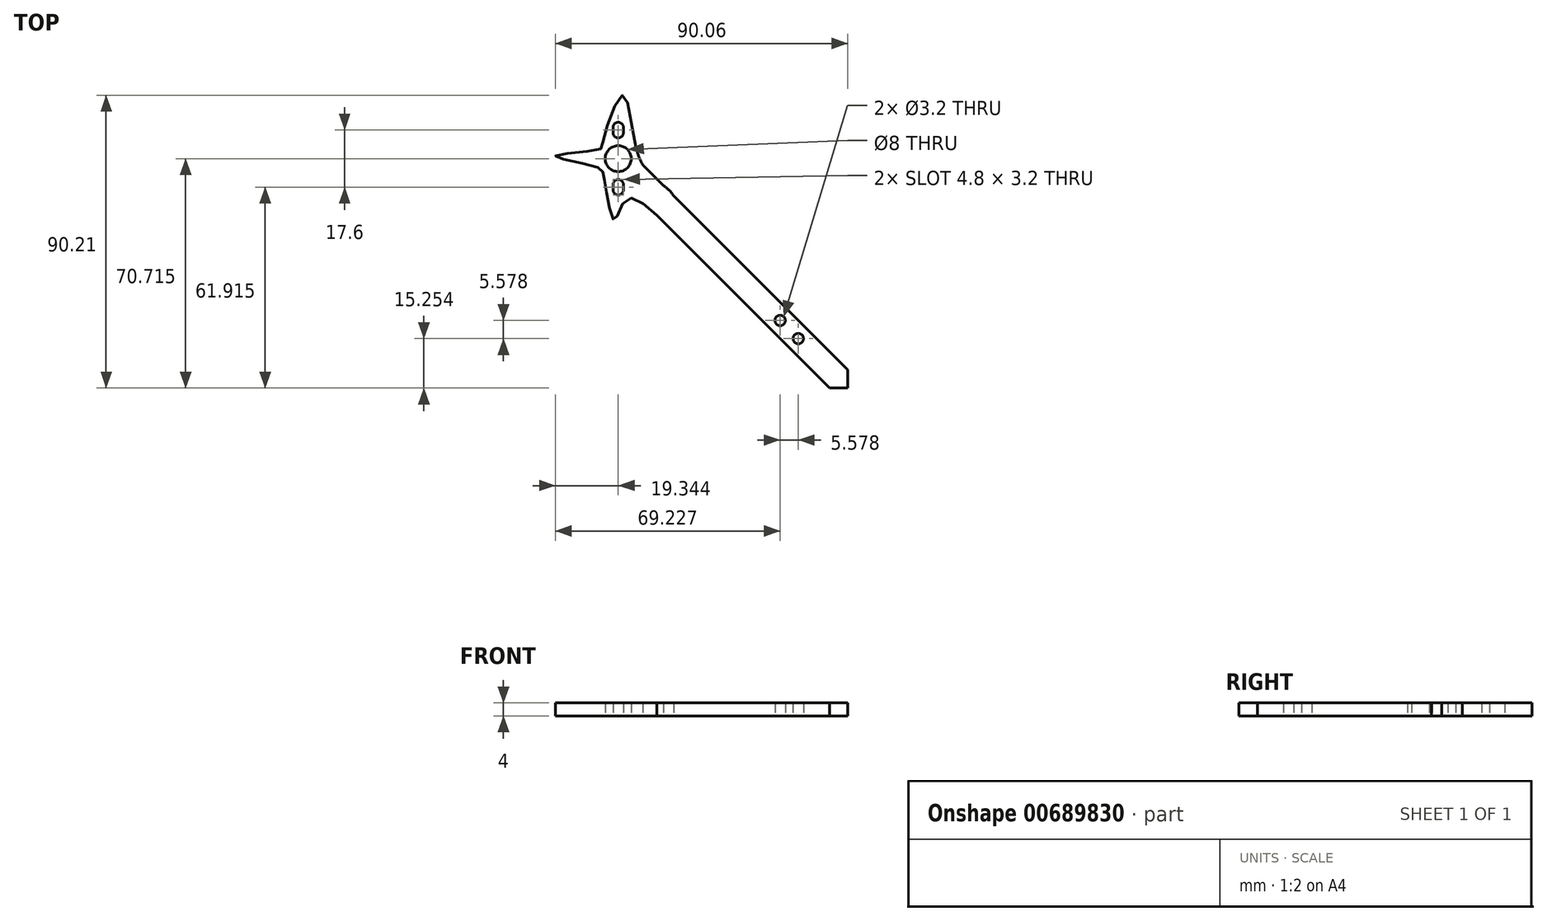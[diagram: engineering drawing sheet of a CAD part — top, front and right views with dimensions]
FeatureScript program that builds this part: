
annotation { "Feature Type Name" : "Feature", "Feature Type Description" : "" }
export const myFeature = defineFeature(function(context is Context, id is Id, definition is map)
    precondition{}
    {
        {
            var Q0;
            Q0=qCreatedBy(makeId("Top.planeOp"),FACE);
            var sketch = newSketch(context, id + "F0", { "sketchPlane" : qUnion([Q0])});
            skLineSegment(sketch, "E0.MirrorCS", {"start": v(4.18, -0.18) * mm, "end": v(-6.4, 10.4) * mm});
            skLineSegment(sketch, "E1.1", {"start": v(4.18, 5.48) * mm, "end": v(-45.9, 55.55) * mm});
            skLineSegment(sketch, "E2.0", {"start": v(-1.48, -0.18) * mm, "end": v(-51.15, 49.49) * mm});
            skCircle(sketch, "E3", {"center": v(-13.11, 17.11) * mm, "radius": 1.6 * mm});
            skCircle(sketch, "E4.MirrorC", {"center": v(-7.53, 11.53) * mm, "radius": 1.6 * mm});
            skLineSegment(sketch, "E5.trimOffspring", {"start": v(-8.67, 12.67) * mm, "end": v(-11.98, 15.98) * mm});
            skCircle(sketch, "E6", {"center": v(-63, 67) * mm, "radius": 4 * mm});
            skArc(sketch, "E7", {"start": v(-61.4, 76.6) * mm, "mid": v(-63, 78.2) * mm, "end": v(-64.6, 76.6) * mm});
            skArc(sketch, "E8", {"start": v(-64.6, 57.4) * mm, "mid": v(-63, 55.8) * mm, "end": v(-61.4, 57.4) * mm});
            skPoint(sketch, "E9", {"position": v(-64.6, 76.6) * mm});
            skPoint(sketch, "E10", {"position": v(-61.4, 76.6) * mm});
            skPoint(sketch, "E11", {"position": v(-61.4, 57.4) * mm});
            skPoint(sketch, "E12", {"position": v(-64.6, 57.4) * mm});
            skPoint(sketch, "E13", {"position": v(-63, 75) * mm});
            skPoint(sketch, "E14", {"position": v(-63, 59) * mm});
            skArc(sketch, "E15", {"start": v(-61.4, 59) * mm, "mid": v(-63, 60.6) * mm, "end": v(-64.6, 59) * mm});
            skArc(sketch, "E16", {"start": v(-64.6, 75) * mm, "mid": v(-63, 73.4) * mm, "end": v(-61.4, 75) * mm});
            skPoint(sketch, "E17", {"position": v(-64.6, 75) * mm});
            skPoint(sketch, "E18", {"position": v(-61.4, 75) * mm});
            skLineSegment(sketch, "E19", {"start": v(-64.6, 75) * mm, "end": v(-64.6, 76.6) * mm});
            skLineSegment(sketch, "E20", {"start": v(-61.4, 76.6) * mm, "end": v(-61.4, 75) * mm});
            skPoint(sketch, "E21", {"position": v(-61.4, 59) * mm});
            skPoint(sketch, "E22", {"position": v(-64.6, 59) * mm});
            skLineSegment(sketch, "E23", {"start": v(-64.6, 59) * mm, "end": v(-64.6, 57.4) * mm});
            skLineSegment(sketch, "E24", {"start": v(-61.4, 57.4) * mm, "end": v(-61.4, 59) * mm});
            skLineSegment(sketch, "E25", {"start": v(-1.48, -0.18) * mm, "end": v(2.06, -3.72) * mm});
            skLineSegment(sketch, "E26", {"start": v(4.18, 5.48) * mm, "end": v(7.72, 1.94) * mm});
            skLineSegment(sketch, "E27", {"start": v(7.72, 1.94) * mm, "end": v(7.72, -3.72) * mm});
            skLineSegment(sketch, "E28", {"start": v(2.06, -3.72) * mm, "end": v(7.72, -3.72) * mm});
            skLineSegment(sketch, "E29", {"start": v(-45.9, 55.55) * mm, "end": v(-55.43, 65.09) * mm});
            skFitSpline(sketch, "E30.trimOffspring", {"points": [v(-45.9, 55.55) * mm, v(-48.32, 58.15) * mm, v(-56.44, 67.18) * mm, v(-61.59, 86.49) * mm, v(-67.81, 71.87) * mm, v(-68.9, 69.8) * mm, v(-82.34, 67.8) * mm, v(-69.62, 64.38) * mm, v(-67.63, 62.58) * mm, v(-66.46, 55.55) * mm, v(-64.11, 48.14) * mm, v(-60.5, 54.46) * mm, v(-51.15, 49.49) * mm], "startDerivative": vector(-36.48, 48) * mm, "endDerivative": vector(117.6, -108.09) * mm});
            skArc(sketch, "E31", {"start": v(-57.56, 70.69) * mm, "mid": v(-56.75, 67.79) * mm, "end": v(-55.43, 65.09) * mm});
            skSolve(sketch);
        }
        {
            var Q0;
            Q0 = qSketchRegion(id + "F0", true);
            extrude(context, id + "F1", {"entities" : qUnion([Q0]), "depth" : 4 * mm, "offsetDistance" : 25 * mm});
        }
    });
